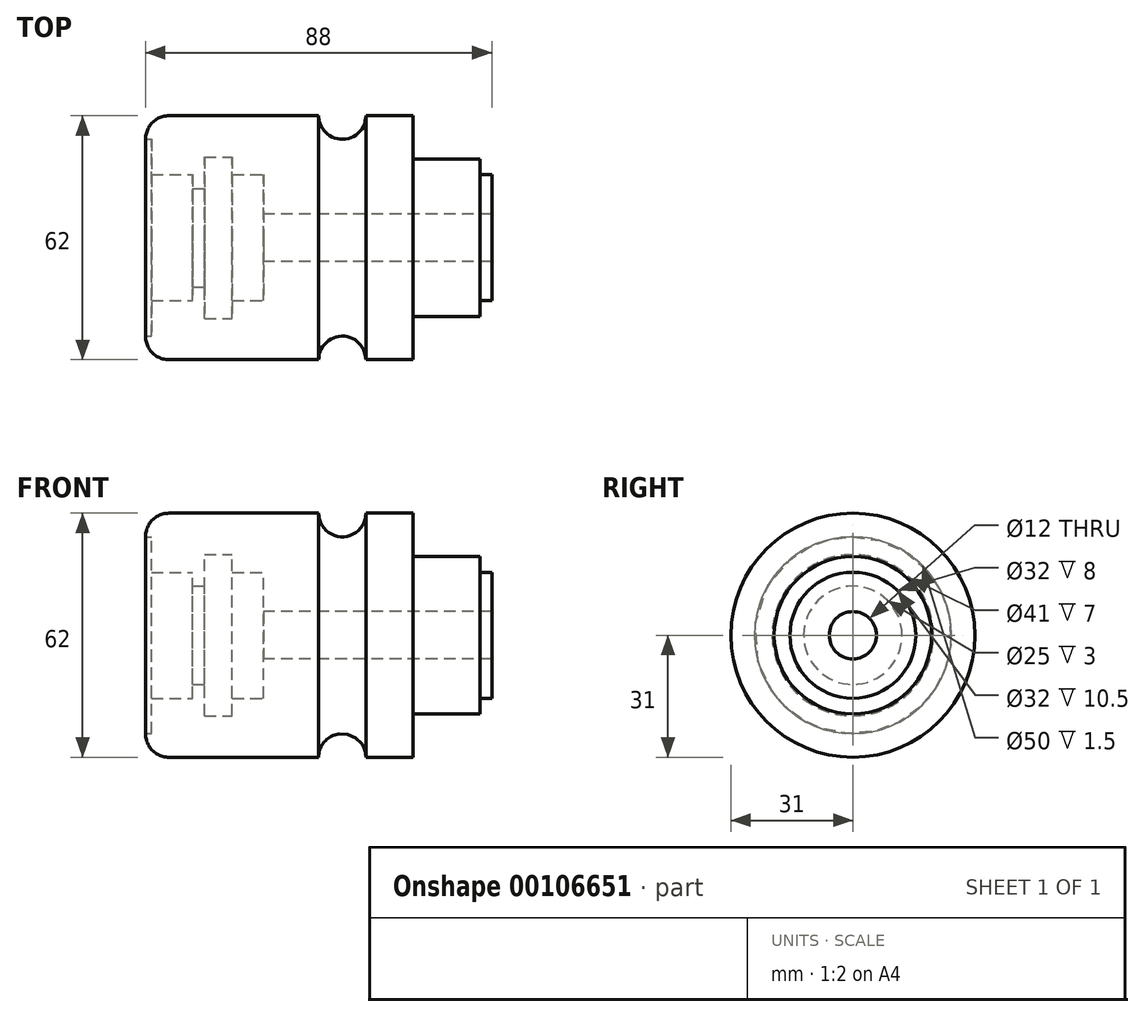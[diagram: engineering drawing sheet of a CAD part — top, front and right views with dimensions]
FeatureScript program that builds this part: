
annotation { "Feature Type Name" : "Feature", "Feature Type Description" : "" }
export const myFeature = defineFeature(function(context is Context, id is Id, definition is map)
    precondition{}
    {
        {
            var Q0;
            Q0=qCreatedBy(makeId("Front.planeOp"),FACE);
            var sketch = newSketch(context, id + "F0", { "sketchPlane" : qUnion([Q0])});
            skLineSegment(sketch, "E0", {"start": v(-105.12, 0) * mm, "end": v(110.17, 0) * mm, "construction": true});
            skLineSegment(sketch, "E1", {"start": v(0, 6) * mm, "end": v(88, 6) * mm});
            skLineSegment(sketch, "E2", {"start": v(88, 6) * mm, "end": v(88, 16) * mm});
            skLineSegment(sketch, "E3", {"start": v(88, 16) * mm, "end": v(85, 16) * mm});
            skLineSegment(sketch, "E4", {"start": v(85, 16) * mm, "end": v(85, 20) * mm});
            skLineSegment(sketch, "E5", {"start": v(85, 20) * mm, "end": v(68, 20) * mm});
            skLineSegment(sketch, "E6", {"start": v(68, 20) * mm, "end": v(68, 31) * mm});
            skLineSegment(sketch, "E7", {"start": v(68, 31) * mm, "end": v(56, 31) * mm});
            skLineSegment(sketch, "E8", {"start": v(44, 31) * mm, "end": v(6, 31) * mm});
            skLineSegment(sketch, "E9", {"start": v(0, 25) * mm, "end": v(0, 6) * mm});
            skArc(sketch, "E10", {"start": v(44, 31) * mm, "mid": v(50, 25) * mm, "end": v(56, 31) * mm});
            skArc(sketch, "E11", {"start": v(6, 31) * mm, "mid": v(1.76, 29.24) * mm, "end": v(0, 25) * mm});
            skLineSegment(sketch, "E12", {"start": v(85, 16) * mm, "end": v(85, 6) * mm});
            skLineSegment(sketch, "E13", {"start": v(68, 20) * mm, "end": v(68, 6) * mm});
            skLineSegment(sketch, "E14", {"start": v(56, 31.25) * mm, "end": v(56, 6) * mm});
            skLineSegment(sketch, "E15", {"start": v(44, 31) * mm, "end": v(44, 6) * mm});
            skSolve(sketch);
        }
        {
            var Q0;
            Q0 = qSketchRegion(id + "F0", true);
            var Q1;
            Q1=sQuery(id+"F0.wireOp",EDGE,"E0");
            revolve(context, id + "F1", {"entities" : qUnion([Q0]), "axis" : qUnion([Q1]), "revolveType" : RevolveType.FULL});
        }
        {
            var Q0;
            Q0=qCreatedBy(makeId("Front.planeOp"),FACE);
            var sketch = newSketch(context, id + "F2", { "sketchPlane" : qUnion([Q0])});
            skLineSegment(sketch, "E16", {"start": v(-60.58, 0) * mm, "end": v(97.47, 0) * mm, "construction": true});
            skLineSegment(sketch, "E17", {"start": v(0, 0) * mm, "end": v(88, 0) * mm});
            skLineSegment(sketch, "E18", {"start": v(88, 0) * mm, "end": v(88, 6) * mm});
            skLineSegment(sketch, "E19", {"start": v(88, 6) * mm, "end": v(30, 6) * mm});
            skLineSegment(sketch, "E20", {"start": v(30, 6) * mm, "end": v(30, 0) * mm});
            skLineSegment(sketch, "E21", {"start": v(30, 0) * mm, "end": v(22, 0) * mm});
            skLineSegment(sketch, "E22", {"start": v(22, 0) * mm, "end": v(22, 16) * mm});
            skLineSegment(sketch, "E23", {"start": v(22, 16) * mm, "end": v(30, 16) * mm});
            skLineSegment(sketch, "E24", {"start": v(30, 16) * mm, "end": v(30, 6) * mm});
            skLineSegment(sketch, "E25", {"start": v(15, 0) * mm, "end": v(22, 0) * mm});
            skLineSegment(sketch, "E26", {"start": v(22, 20.5) * mm, "end": v(15, 20.5) * mm});
            skLineSegment(sketch, "E27", {"start": v(15, 20.5) * mm, "end": v(15, 0) * mm});
            skLineSegment(sketch, "E28", {"start": v(15, 0) * mm, "end": v(12, 0) * mm});
            skLineSegment(sketch, "E29", {"start": v(12, 0) * mm, "end": v(12, 12.5) * mm});
            skLineSegment(sketch, "E30", {"start": v(12, 12.5) * mm, "end": v(15, 12.5) * mm});
            skLineSegment(sketch, "E31", {"start": v(15, 12.5) * mm, "end": v(15, 0) * mm});
            skLineSegment(sketch, "E32", {"start": v(22, 20.5) * mm, "end": v(22, 0) * mm});
            skLineSegment(sketch, "E33", {"start": v(12, 0) * mm, "end": v(12, 16) * mm});
            skLineSegment(sketch, "E34", {"start": v(12, 16) * mm, "end": v(1.5, 16) * mm});
            skLineSegment(sketch, "E35", {"start": v(1.5, 16) * mm, "end": v(1.5, 0) * mm});
            skLineSegment(sketch, "E36", {"start": v(1.5, 0) * mm, "end": v(12, 0) * mm});
            skLineSegment(sketch, "E37", {"start": v(1.5, 0) * mm, "end": v(1.5, 25) * mm});
            skLineSegment(sketch, "E38", {"start": v(1.5, 25) * mm, "end": v(0, 25) * mm});
            skLineSegment(sketch, "E39", {"start": v(0, 25) * mm, "end": v(0, 0) * mm});
            skLineSegment(sketch, "E40", {"start": v(1.5, 0) * mm, "end": v(0, 0) * mm});
            skSolve(sketch);
        }
        {
            var Q0;
            Q0 = qSketchRegion(id + "F2", true);
            var Q1;
            Q1=sQuery(id+"F2.wireOp",EDGE,"E17");
            revolve(context, id + "F3", {"operationType" : NewBodyOperationType.REMOVE, "entities" : qUnion([Q0]), "axis" : qUnion([Q1]), "revolveType" : RevolveType.FULL, "oppositeDirection" : true});
        }
    });
